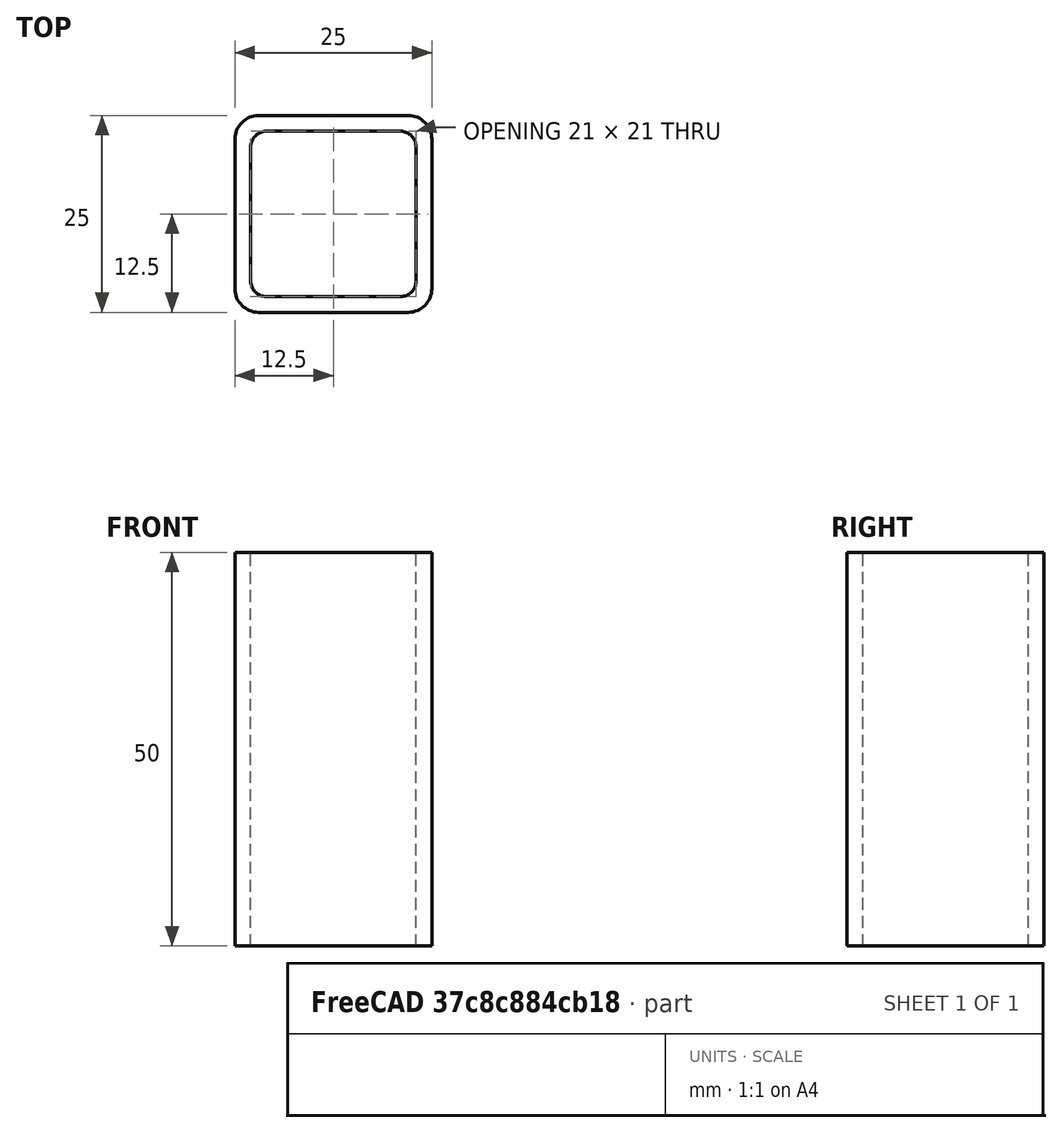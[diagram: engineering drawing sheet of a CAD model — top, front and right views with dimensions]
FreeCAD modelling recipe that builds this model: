
FCSTD DOCUMENT  (FreeCAD 0.15R4671 (Git))
Label: Square hollow section 25x25x2 EN10219 S235JRH
License: All rights reserved
LicenseURL: http://en.wikipedia.org/wiki/All_rights_reserved
objects: Sketcher::SketchObject×1, Part::Extrusion×1
note: 2 computed .brp shape members not serialized (recipe doc carries the construction recipe); baked Part::Feature solids carry a one-line shape summary decoded from their .brp

FEATURE [Sketcher::SketchObject] Sketch
  sketch-geometry (16):
    g0: LineSegment StartX=-8.5 StartY=10.5 StartZ=0 EndX=8.5 EndY=10.5 EndZ=0
    g1: LineSegment StartX=10.5 StartY=8.5 StartZ=0 EndX=10.5 EndY=-8.5 EndZ=0
    g2: LineSegment StartX=8.5 StartY=-10.5 StartZ=0 EndX=-8.5 EndY=-10.5 EndZ=0
    g3: LineSegment StartX=-10.5 StartY=-8.5 StartZ=0 EndX=-10.5 EndY=8.5 EndZ=0
    g4: LineSegment StartX=-9.5 StartY=12.5 StartZ=0 EndX=9.5 EndY=12.5 EndZ=0
    g5: LineSegment StartX=12.5 StartY=9.5 StartZ=0 EndX=12.5 EndY=-9.5 EndZ=0
    g6: LineSegment StartX=9.5 StartY=-12.5 StartZ=0 EndX=-9.5 EndY=-12.5 EndZ=0
    g7: LineSegment StartX=-12.5 StartY=-9.5 StartZ=0 EndX=-12.5 EndY=9.5 EndZ=0
    g8: ArcOfCircle CenterX=-8.5 CenterY=8.5 CenterZ=0 NormalX=0 NormalY=0 NormalZ=1 Radius=2 StartAngle=1.5708 EndAngle=3.14159
    g9: ArcOfCircle CenterX=8.5 CenterY=8.5 CenterZ=0 NormalX=0 NormalY=0 NormalZ=1 Radius=2 StartAngle=2e-12 EndAngle=1.5708
    g10: ArcOfCircle CenterX=8.5 CenterY=-8.5 CenterZ=0 NormalX=0 NormalY=0 NormalZ=1 Radius=2 StartAngle=4.71239 EndAngle=6.28319
    g11: ArcOfCircle CenterX=-8.5 CenterY=-8.5 CenterZ=0 NormalX=0 NormalY=0 NormalZ=1 Radius=2 StartAngle=3.14159 EndAngle=4.71239
    g12: ArcOfCircle CenterX=9.5 CenterY=9.5 CenterZ=0 NormalX=0 NormalY=0 NormalZ=1 Radius=3 StartAngle=0 EndAngle=1.5708
    g13: ArcOfCircle CenterX=9.5 CenterY=-9.5 CenterZ=0 NormalX=0 NormalY=0 NormalZ=1 Radius=3 StartAngle=4.71239 EndAngle=6.28319
    g14: ArcOfCircle CenterX=-9.5 CenterY=-9.5 CenterZ=0 NormalX=0 NormalY=0 NormalZ=1 Radius=3 StartAngle=3.14159 EndAngle=4.71239
    g15: ArcOfCircle CenterX=-9.5 CenterY=9.5 CenterZ=0 NormalX=0 NormalY=0 NormalZ=1 Radius=3 StartAngle=1.5708 EndAngle=3.14159
  constraints (36):
    c: Horizontal(g2)
    c: Vertical(g3)
    c: Horizontal(g6)
    c: Vertical(g7)
    c: Tangent(g3,g8) = 1.5708
    c: Tangent(g0,g8) = 1.5708
    c: Tangent(g0,g9) = 1.5708
    c: Tangent(g1,g9) = 1.5708
    c: Tangent(g1,g10) = 1.5708
    c: Tangent(g2,g10) = 1.5708
    c: Tangent(g2,g11) = 1.5708
    c: Tangent(g3,g11) = 1.5708
    c: Tangent(g4,g12) = 1.5708
    c: Tangent(g5,g12) = 1.5708
    c: Tangent(g5,g13) = 1.5708
    c: Tangent(g6,g13) = 1.5708
    c: Tangent(g6,g14) = 1.5708
    c: Tangent(g7,g14) = 1.5708
    c: Tangent(g7,g15) = 1.5708
    c: Tangent(g4,g15) = 1.5708
    c: Equal(g9,g8)
    c: Equal(g9,g11)
    c: Equal(g9,g10)
    c: Equal(g12,g15)
    c: Equal(g12,g14)
    c: Equal(g12,g13)
    c: Symmetric(g4,g6,g-1)
    c: Symmetric(g7,g5,g-2)
    c: DistanceY(g4,g6) = -25
    c: DistanceX(g7,g5) = 25
    c: Symmetric(g3,g1,g-2)
    c: Symmetric(g0,g2,g-1)
    c: DistanceY(g0,g4) = 2
    c: DistanceX(g5,g1) = -2
    c: Radius(g9) = 2
    c: Radius(g12) = 3
FEATURE [Part::Extrusion] Extrude  label="Square hollow section 25x25x2 EN10219 S235JRH"
  Base = -> Sketch
  Dir = (0,0,50)
  Solid = true
